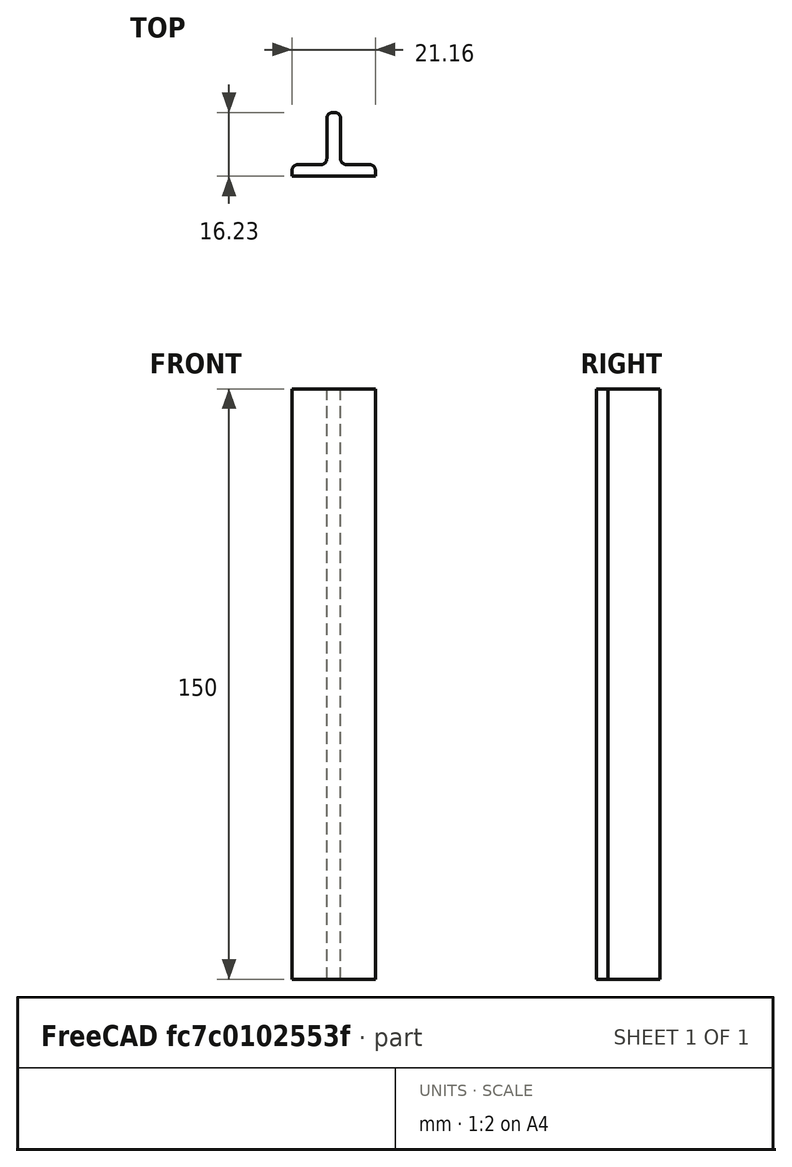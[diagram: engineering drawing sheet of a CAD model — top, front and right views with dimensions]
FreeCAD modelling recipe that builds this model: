
FCSTD DOCUMENT  (FreeCAD 0.18R16146 (Git))
Label: kitty-off-150mm
License: All rights reserved
LicenseURL: http://en.wikipedia.org/wiki/All_rights_reserved
objects: Sketcher::SketchObject×1, PartDesign::Pad×1, PartDesign::Body×1
note: 4 computed .brp shape members not serialized (recipe doc carries the construction recipe); baked Part::Feature solids carry a one-line shape summary decoded from their .brp

FEATURE [Sketcher::SketchObject] Sketch001
  MapMode = 5
  Support = -> [XY_Plane001]
  sketch-geometry (14):
    g0: LineSegment StartX=-40 StartY=-16 StartZ=0 EndX=-30.9581 EndY=-16 EndZ=0
    g1: LineSegment StartX=-16.3192 StartY=-19.4722 StartZ=0 EndX=-41.4746 EndY=-19.4722 EndZ=0
    g2: LineSegment StartX=-29.483 StartY=-14.5248 StartZ=0 EndX=-29.483 EndY=2.69423 EndZ=0
    g3: LineSegment StartX=-28.0078 StartY=1.21905 StartZ=0 EndX=-29.786 EndY=1.21905 EndZ=0
    g4: LineSegment StartX=-28.3108 StartY=2.69423 StartZ=0 EndX=-28.3108 EndY=-14.5248 EndZ=0
    g5: LineSegment StartX=-26.8357 StartY=-16 StartZ=0 EndX=-17.7938 EndY=-16 EndZ=0
    g6: ArcOfCircle CenterX=-28.0078 CenterY=2.69423 CenterZ=0 NormalX=0 NormalY=0 NormalZ=1 AngleXU=0 Radius=1.47518 StartAngle=4.71239 EndAngle=9.42478
    g7: ArcOfCircle CenterX=-29.786 CenterY=2.69423 CenterZ=0 NormalX=0 NormalY=0 NormalZ=1 AngleXU=0 Radius=1.47518 StartAngle=0 EndAngle=4.71239
    g8: ArcOfCircle CenterX=-26.8357 CenterY=-14.5248 CenterZ=0 NormalX=0 NormalY=0 NormalZ=1 AngleXU=0 Radius=1.47518 StartAngle=3.14159 EndAngle=4.71239
    g9: ArcOfCircle CenterX=-30.9581 CenterY=-14.5248 CenterZ=0 NormalX=0 NormalY=0 NormalZ=1 AngleXU=0 Radius=1.47518 StartAngle=4.71239 EndAngle=6.28319
    g10: LineSegment StartX=-16.3192 StartY=-19.4722 StartZ=0 EndX=-16.3192 EndY=-17.4746 EndZ=0
    g11: LineSegment StartX=-41.4746 StartY=-19.4722 StartZ=0 EndX=-41.4746 EndY=-17.4746 EndZ=0
    g12: ArcOfCircle CenterX=-40 CenterY=-17.4746 CenterZ=0 NormalX=0 NormalY=0 NormalZ=1 AngleXU=0 Radius=1.47462 StartAngle=1.5708 EndAngle=3.14159
    g13: ArcOfCircle CenterX=-17.7938 CenterY=-17.4746 CenterZ=0 NormalX=0 NormalY=0 NormalZ=1 AngleXU=0 Radius=1.47462 StartAngle=0 EndAngle=1.5708
  constraints (29):
    c: Horizontal(g1)
    c: Tangent(g2,g6) = 1.5708
    c: Tangent(g3,g6) = 1.5708
    c: Tangent(g3,g7) = 1.5708
    c: Tangent(g4,g7) = 1.5708
    c: Horizontal(g3)
    c: Vertical(g2)
    c: Vertical(g4)
    c: Equal(g6,g7)
    c: Tangent(g5,g8) = -1.5708
    c: Tangent(g4,g8) = -1.5708
    c: Tangent(g2,g9) = -1.5708
    c: Tangent(g0,g9) = -1.5708
    c: Equal(g9,g8)
    c: Equal(g0,g5)
    c: Horizontal(g0)
    c: Horizontal(g5)
    c: Equal(g11,g10)
    c: Tangent(g11,g12) = 1.5708
    c: Tangent(g0,g12) = 1.5708
    c: Vertical(g11)
    c: Vertical(g10)
    c: Tangent(g5,g13) = 1.5708
    c: Tangent(g10,g13) = -1.5708
    c: Coincident(g11,g1)
    c: Coincident(g1,g10)
    c: Equal(g12,g13)
    c: Equal(g0,g5)
    c: Equal(g9,g6)
FEATURE [PartDesign::Pad] Pad
  Length = 150
  Length2 = 43
  Profile = -> Sketch001
  Type = 0
FEATURE [PartDesign::Body] Body001
  Group = -> [Sketch001,Pad]
  Origin = -> Origin001
  Tip = -> Pad
